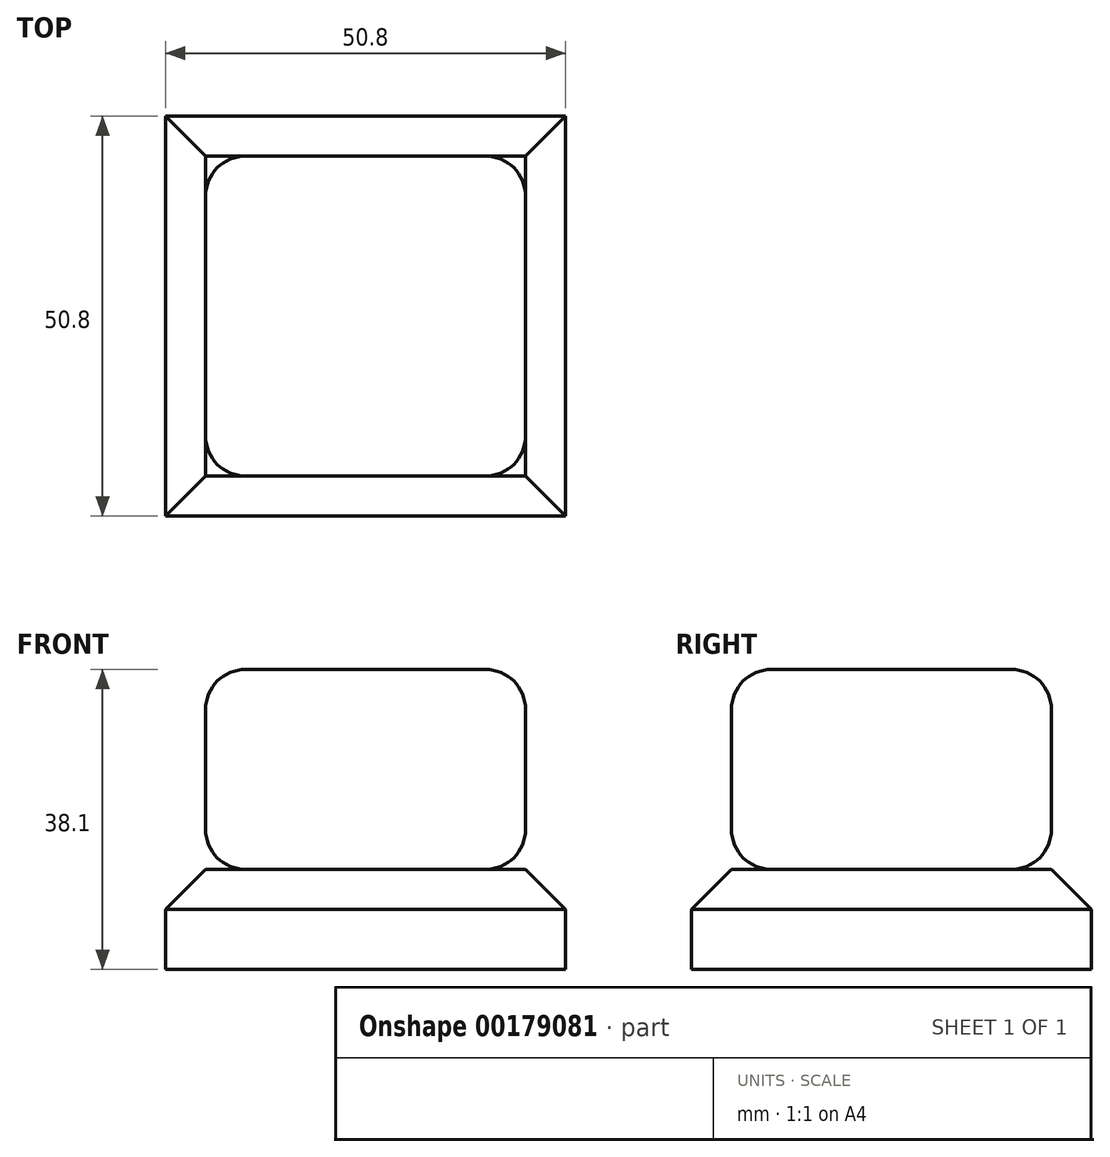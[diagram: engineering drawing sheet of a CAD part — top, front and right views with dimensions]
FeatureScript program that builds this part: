
annotation { "Feature Type Name" : "Feature", "Feature Type Description" : "" }
export const myFeature = defineFeature(function(context is Context, id is Id, definition is map)
    precondition{}
    {
        {
            var Q0;
            Q0=qCreatedBy(makeId("Top.planeOp"),FACE);
            var sketch = newSketch(context, id + "F0", { "sketchPlane" : qUnion([Q0])});
            skLineSegment(sketch, "E0.bottom", {"start": v(-53.15, 23.2) * mm, "end": v(-2.35, 23.2) * mm});
            skLineSegment(sketch, "E0.top", {"start": v(-53.15, -27.6) * mm, "end": v(-2.35, -27.6) * mm});
            skLineSegment(sketch, "E0.left", {"start": v(-53.15, 23.2) * mm, "end": v(-53.15, -27.6) * mm});
            skLineSegment(sketch, "E0.right", {"start": v(-2.35, 23.2) * mm, "end": v(-2.35, -27.6) * mm});
            skSolve(sketch);
        }
        {
            var Q0;
            Q0=makeQuery(id+"F0.imprint","IMPRINT",FACE,{"disambiguationData":[TD([[makeQuery(id+"F0.imprint","IMPRINT",EDGE,{"derivedFrom":sQuery(id+"F0.wireOp",EDGE,"E0.bottom")}),-1.0]])]});
            extrude(context, id + "F1", {"entities" : qUnion([Q0]), "depth" : 12.7 * mm});
        }
        {
            var Q0;
            Q0=makeQuery(id+"F1.opExtrude","CAP_EDGE",EDGE,{"disambiguationData":[OSD([sQuery(id+"F0.wireOp",EDGE,"E0.top")])],"isStart":false});
            var Q1;
            Q1=makeQuery(id+"F1.opExtrude","CAP_EDGE",EDGE,{"disambiguationData":[OSD([sQuery(id+"F0.wireOp",EDGE,"E0.right")])],"isStart":false});
            var Q2;
            Q2=makeQuery(id+"F1.opExtrude","CAP_EDGE",EDGE,{"disambiguationData":[OSD([sQuery(id+"F0.wireOp",EDGE,"E0.bottom")])],"isStart":false});
            var Q3;
            Q3=makeQuery(id+"F1.opExtrude","CAP_EDGE",EDGE,{"disambiguationData":[OSD([sQuery(id+"F0.wireOp",EDGE,"E0.left")])],"isStart":false});
            chamfer(context, id + "F2", {"entities" : qUnion([Q0, Q1, Q2, Q3]), "width" : 5.08 * mm, "tangentPropagation" : true});
        }
        {
            var Q0;
            Q0=makeQuery(id+"F1.opExtrude","CAP_FACE",FACE,{"disambiguationData":[OSD([sQuery(id+"F0.wireOp",EDGE,"E0.bottom"),sQuery(id+"F0.wireOp",EDGE,"E0.top"),sQuery(id+"F0.wireOp",EDGE,"E0.left"),sQuery(id+"F0.wireOp",EDGE,"E0.right")])],"isStart":false});
            extrude(context, id + "F3", {"entities" : qUnion([Q0]), "depth" : 25.4 * mm});
        }
        {
            var Q0;
            {var subQ0=sQuery(id+"F0.wireOp",EDGE,"E0.right");var subQ1=sQuery(id+"F0.wireOp",EDGE,"E0.left");var subQ2=sQuery(id+"F0.wireOp",EDGE,"E0.top");var subQ3=sQuery(id+"F0.wireOp",EDGE,"E0.bottom");Q0=makeQuery(id+"F3.opExtrude","SWEPT_FACE",FACE,{"disambiguationData":[OSD([subQ3,subQ2,subQ1,subQ0]),TDD([makeQuery(id+"F2.opChamfer","BLEND_EDGE",EDGE,{"blendedFrom":[makeQuery(id+"F1.opExtrude","CAP_EDGE",EDGE,{"disambiguationData":[OSD([subQ0])],"isStart":false}),makeQuery(id+"F1.opExtrude","CAP_FACE",FACE,{"disambiguationData":[OSD([subQ3,subQ2,subQ1,subQ0])],"isStart":false})],"blendedInto":[makeQuery(id+"F1.opExtrude","CAP_FACE",FACE,{"disambiguationData":[OSD([subQ3,subQ2,subQ1,subQ0])],"isStart":false})]})])]});}
            var Q1;
            {var subQ0=sQuery(id+"F0.wireOp",EDGE,"E0.right");var subQ1=sQuery(id+"F0.wireOp",EDGE,"E0.left");var subQ2=sQuery(id+"F0.wireOp",EDGE,"E0.top");var subQ3=sQuery(id+"F0.wireOp",EDGE,"E0.bottom");Q1=makeQuery(id+"F3.opExtrude","SWEPT_FACE",FACE,{"disambiguationData":[OSD([subQ3,subQ2,subQ1,subQ0]),TDD([makeQuery(id+"F2.opChamfer","BLEND_EDGE",EDGE,{"blendedFrom":[makeQuery(id+"F1.opExtrude","CAP_EDGE",EDGE,{"disambiguationData":[OSD([subQ3])],"isStart":false}),makeQuery(id+"F1.opExtrude","CAP_FACE",FACE,{"disambiguationData":[OSD([subQ3,subQ2,subQ1,subQ0])],"isStart":false})],"blendedInto":[makeQuery(id+"F1.opExtrude","CAP_FACE",FACE,{"disambiguationData":[OSD([subQ3,subQ2,subQ1,subQ0])],"isStart":false})]})])]});}
            var Q2;
            {var subQ0=sQuery(id+"F0.wireOp",EDGE,"E0.right");var subQ1=sQuery(id+"F0.wireOp",EDGE,"E0.left");var subQ2=sQuery(id+"F0.wireOp",EDGE,"E0.top");var subQ3=sQuery(id+"F0.wireOp",EDGE,"E0.bottom");Q2=makeQuery(id+"F3.opExtrude","SWEPT_FACE",FACE,{"disambiguationData":[OSD([subQ3,subQ2,subQ1,subQ0]),TDD([makeQuery(id+"F2.opChamfer","BLEND_EDGE",EDGE,{"blendedFrom":[makeQuery(id+"F1.opExtrude","CAP_EDGE",EDGE,{"disambiguationData":[OSD([subQ1])],"isStart":false}),makeQuery(id+"F1.opExtrude","CAP_FACE",FACE,{"disambiguationData":[OSD([subQ3,subQ2,subQ1,subQ0])],"isStart":false})],"blendedInto":[makeQuery(id+"F1.opExtrude","CAP_FACE",FACE,{"disambiguationData":[OSD([subQ3,subQ2,subQ1,subQ0])],"isStart":false})]})])]});}
            var Q3;
            {var subQ0=sQuery(id+"F0.wireOp",EDGE,"E0.right");var subQ1=sQuery(id+"F0.wireOp",EDGE,"E0.left");var subQ2=sQuery(id+"F0.wireOp",EDGE,"E0.top");var subQ3=sQuery(id+"F0.wireOp",EDGE,"E0.bottom");Q3=makeQuery(id+"F3.opExtrude","SWEPT_FACE",FACE,{"disambiguationData":[OSD([subQ3,subQ2,subQ1,subQ0]),TDD([makeQuery(id+"F2.opChamfer","BLEND_EDGE",EDGE,{"blendedFrom":[makeQuery(id+"F1.opExtrude","CAP_EDGE",EDGE,{"disambiguationData":[OSD([subQ2])],"isStart":false}),makeQuery(id+"F1.opExtrude","CAP_FACE",FACE,{"disambiguationData":[OSD([subQ3,subQ2,subQ1,subQ0])],"isStart":false})],"blendedInto":[makeQuery(id+"F1.opExtrude","CAP_FACE",FACE,{"disambiguationData":[OSD([subQ3,subQ2,subQ1,subQ0])],"isStart":false})]})])]});}
            fillet(context, id + "F4", {"entities" : qUnion([Q0, Q1, Q2, Q3]), "radius" : 5.08 * mm, "tangentPropagation" : true, "allowEdgeOverflow" : false});
        }
    });
